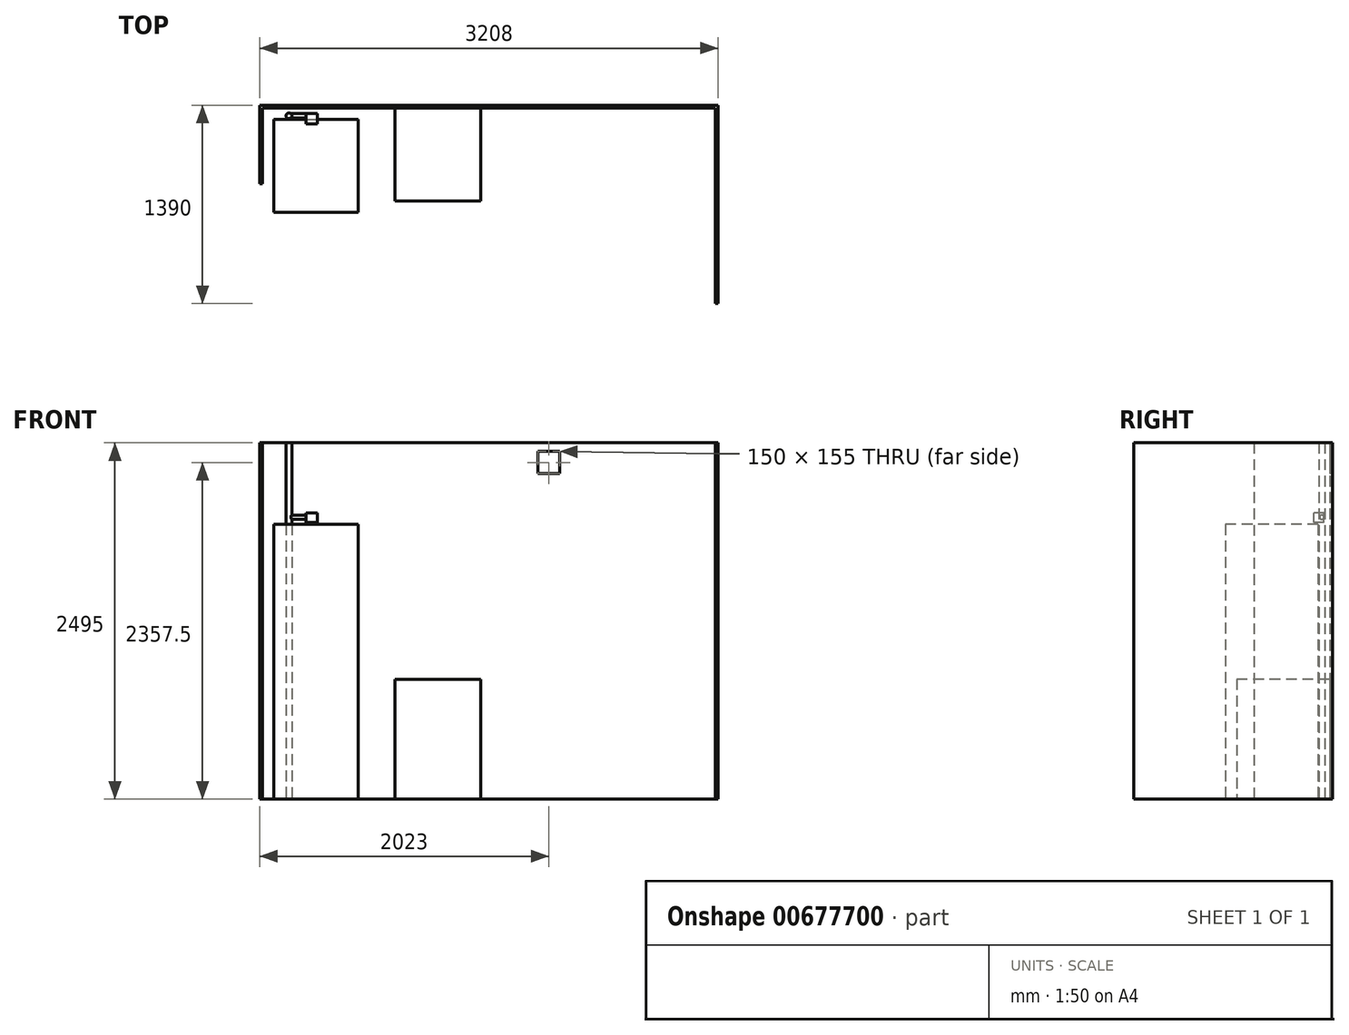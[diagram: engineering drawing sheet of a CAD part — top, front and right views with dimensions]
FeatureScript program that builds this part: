
annotation { "Feature Type Name" : "Feature", "Feature Type Description" : "" }
export const myFeature = defineFeature(function(context is Context, id is Id, definition is map)
    precondition{}
    {
        {
            var Q0;
            Q0=qCreatedBy(makeId("Top.planeOp"),FACE);
            var sketch = newSketch(context, id + "F0", { "sketchPlane" : qUnion([Q0])});
            skLineSegment(sketch, "E0.top", {"start": v(0, 530) * mm, "end": v(3168, 530) * mm});
            skLineSegment(sketch, "E0.left", {"start": v(0, 0) * mm, "end": v(0, 530) * mm});
            skLineSegment(sketch, "E0.right", {"start": v(3168, -840) * mm, "end": v(3168, 530) * mm});
            skLineSegment(sketch, "E1.0", {"start": v(-20, 0) * mm, "end": v(-20, 550) * mm});
            skLineSegment(sketch, "E1.1", {"start": v(-20, 550) * mm, "end": v(3188, 550) * mm});
            skLineSegment(sketch, "E1.2", {"start": v(3188, -840) * mm, "end": v(3188, 550) * mm});
            skLineSegment(sketch, "E2", {"start": v(-20, 0) * mm, "end": v(0, 0) * mm});
            skLineSegment(sketch, "E3", {"start": v(3168, -840) * mm, "end": v(3188, -840) * mm});
            skSolve(sketch);
        }
        {
            var Q0;
            Q0 = qSketchRegion(id + "F0", true);
            extrude(context, id + "F1", {"entities" : qUnion([Q0]), "depth" : 2495 * mm, "offsetDistance" : 25 * mm});
        }
        {
            var Q0;
            Q0=makeQuery(id+"F1.opExtrude","SWEPT_FACE",FACE,{"disambiguationData":[OSD([sQuery(id+"F0.wireOp",EDGE,"E0.top")])]});
            var sketch = newSketch(context, id + "F2", { "sketchPlane" : qUnion([Q0])});
            skLineSegment(sketch, "E4.bottom", {"start": v(2078, 2435) * mm, "end": v(1928, 2435) * mm});
            skLineSegment(sketch, "E4.top", {"start": v(2078, 2280) * mm, "end": v(1928, 2280) * mm});
            skLineSegment(sketch, "E4.left", {"start": v(2078, 2435) * mm, "end": v(2078, 2280) * mm});
            skLineSegment(sketch, "E4.right", {"start": v(1928, 2435) * mm, "end": v(1928, 2280) * mm});
            skSolve(sketch);
        }
        {
            var Q0;
            Q0 = qSketchRegion(id + "F2", true);
            extrude(context, id + "F3", {"entities" : qUnion([Q0]), "operationType" : NewBodyOperationType.REMOVE, "oppositeDirection" : true, "depth" : 25 * mm, "offsetDistance" : 25 * mm});
        }
        {
            var Q0;
            Q0=qCreatedBy(makeId("Top.planeOp"),FACE);
            var sketch = newSketch(context, id + "F4", { "sketchPlane" : qUnion([Q0])});
            skLineSegment(sketch, "E5.top", {"start": v(78, -200) * mm, "end": v(668, -200) * mm});
            skLineSegment(sketch, "E5.left", {"start": v(78, 450) * mm, "end": v(78, -200) * mm});
            skLineSegment(sketch, "E5.right", {"start": v(668, 450) * mm, "end": v(668, -200) * mm});
            skLineSegment(sketch, "E6.0", {"start": v(78, 450) * mm, "end": v(668, 450) * mm});
            skPoint(sketch, "E7.start.orphan", {"position": v(78, 530) * mm});
            skPoint(sketch, "E8.orphan", {"position": v(668, 530) * mm});
            skSolve(sketch);
        }
        {
            var Q0;
            Q0 = qSketchRegion(id + "F4", true);
            extrude(context, id + "F5", {"entities" : qUnion([Q0]), "depth" : 1925 * mm, "offsetDistance" : 25 * mm});
        }
        {
            var Q0;
            Q0=qCreatedBy(makeId("Top.planeOp"),FACE);
            var sketch = newSketch(context, id + "F6", { "sketchPlane" : qUnion([Q0])});
            skLineSegment(sketch, "E9.bottom", {"start": v(928, 530) * mm, "end": v(1528, 530) * mm});
            skLineSegment(sketch, "E9.top", {"start": v(928, -120) * mm, "end": v(1528, -120) * mm});
            skLineSegment(sketch, "E9.left", {"start": v(928, 530) * mm, "end": v(928, -120) * mm});
            skLineSegment(sketch, "E9.right", {"start": v(1528, 530) * mm, "end": v(1528, -120) * mm});
            skSolve(sketch);
        }
        {
            var Q0;
            Q0 = qSketchRegion(id + "F6", true);
            extrude(context, id + "F7", {"entities" : qUnion([Q0]), "depth" : 840 * mm, "offsetDistance" : 25 * mm});
        }
        {
            var Q0;
            Q0=qCreatedBy(makeId("Top.planeOp"),FACE);
            var sketch = newSketch(context, id + "F8", { "sketchPlane" : qUnion([Q0])});
            skCircle(sketch, "E10", {"center": v(185, 475) * mm, "radius": 20 * mm});
            skSolve(sketch);
        }
        {
            var Q0;
            Q0 = qSketchRegion(id + "F8", true);
            var Q1;
            Q1=makeQuery(id+"F1.opExtrude","CAP_VERTEX",VERTEX,{"disambiguationData":[OSD([sQuery(id+"F0.wireOp",EDGE,"E0.top"),sQuery(id+"F0.wireOp",EDGE,"E0.left")])],"isStart":false});
            extrude(context, id + "F9", {"entities" : qUnion([Q0]), "operationType" : NewBodyOperationType.ADD, "endBound" : BoundingType.UP_TO_VERTEX, "depth" : 25 * mm, "endBoundEntityVertex" : qUnion([Q1]), "offsetDistance" : 25 * mm});
        }
        {
            var Q0;
            Q0=makeQuery(id+"F1.opExtrude","SWEPT_FACE",FACE,{"disambiguationData":[OSD([sQuery(id+"F0.wireOp",EDGE,"E0.left")])]});
            cPlane(context, id + "F10", {"entities" : qUnion([Q0]), "cplaneType" : CPlaneType.OFFSET, "offset" : 185 * mm, "width" : 150 * mm, "height" : 150 * mm});
        }
        {
            var Q0;
            Q0=qCreatedBy(id+"F10.planeOp",FACE);
            var sketch = newSketch(context, id + "F11", { "sketchPlane" : qUnion([Q0])});
            skLineSegment(sketch, "E11.0", {"start": v(455, 2495) * mm, "end": v(495, 2495) * mm});
            skLineSegment(sketch, "E12", {"start": v(475, 2495) * mm, "end": v(475, 1975) * mm});
            skCircle(sketch, "E13", {"center": v(475, 1975) * mm, "radius": 15 * mm});
            skSolve(sketch);
        }
        {
            var Q0;
            Q0 = qSketchRegion(id + "F11", true);
            extrude(context, id + "F12", {"entities" : qUnion([Q0]), "operationType" : NewBodyOperationType.ADD, "depth" : 200 * mm, "offsetDistance" : 25 * mm});
        }
        {
            var Q0;
            Q0=makeQuery(id+"F12.opExtrude","CAP_FACE",FACE,{"disambiguationData":[OSD([sQuery(id+"F11.wireOp",EDGE,"E13")])],"isStart":false});
            var sketch = newSketch(context, id + "F13", { "sketchPlane" : qUnion([Q0])});
            skLineSegment(sketch, "E14.bottom", {"start": v(490, 1937) * mm, "end": v(420, 1937) * mm});
            skLineSegment(sketch, "E14.top", {"start": v(490, 2005) * mm, "end": v(420, 2005) * mm});
            skLineSegment(sketch, "E14.left", {"start": v(490, 1937) * mm, "end": v(490, 2005) * mm});
            skLineSegment(sketch, "E14.right", {"start": v(420, 1937) * mm, "end": v(420, 2005) * mm});
            skLineSegment(sketch, "E15", {"start": v(420, 1971) * mm, "end": v(250.84, 1971) * mm});
            skSolve(sketch);
        }
        {
            var Q0;
            Q0 = qSketchRegion(id + "F13", true);
            extrude(context, id + "F14", {"entities" : qUnion([Q0]), "operationType" : NewBodyOperationType.ADD, "oppositeDirection" : true, "depth" : 80 * mm, "offsetDistance" : 25 * mm});
        }
    });
